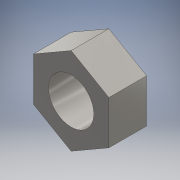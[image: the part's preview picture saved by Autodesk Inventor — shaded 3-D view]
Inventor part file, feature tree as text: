
AUTODESK INVENTOR PART (.ipt)
format: ipt  version: 2016 (Build 200138000, 138)  size: 115,712 bytes
history: native  units: mm
features: extrude x1, sketch x1
ambient origin geometry x8: Origin, YZ Plane, XZ Plane, XY Plane, X Axis, Y Axis, Z Axis, Center Point
bodies: Solid1 (feature_tree)
feature tree (2):
  extrude  "Extrusion1"  Depth=10.0mm
  sketch  "Sketch1"  dims[d0=6.0mm d1=10.0mm d2=5.0mm d3=0.0mm]
